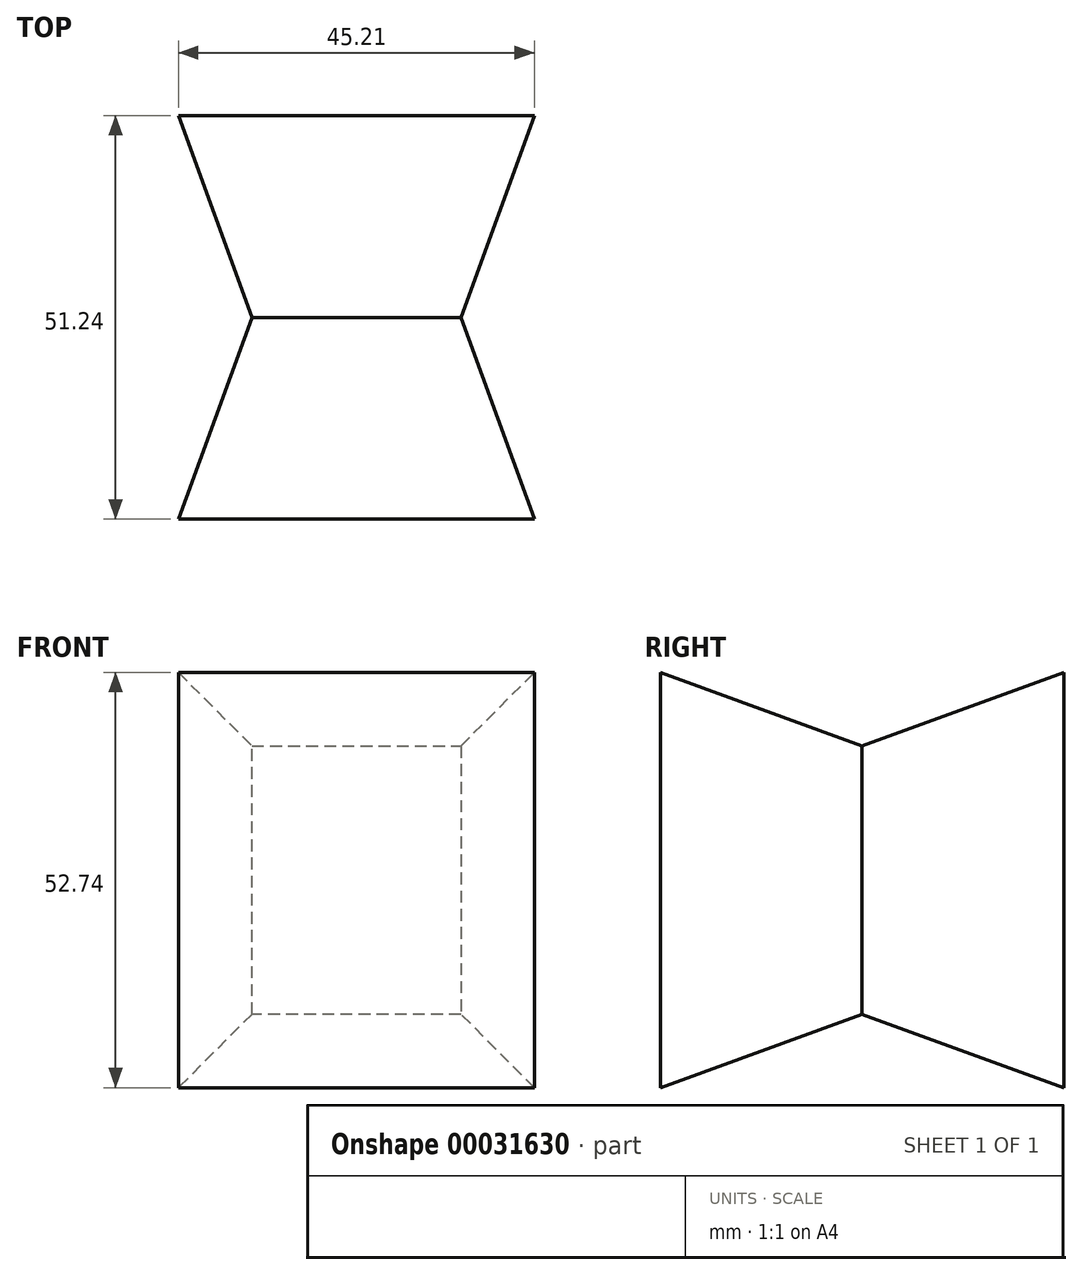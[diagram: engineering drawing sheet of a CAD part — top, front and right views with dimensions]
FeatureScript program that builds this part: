
annotation { "Feature Type Name" : "Feature", "Feature Type Description" : "" }
export const myFeature = defineFeature(function(context is Context, id is Id, definition is map)
    precondition{}
    {
        {
            var Q0;
            Q0=qCreatedBy(makeId("Front.planeOp"),FACE);
            var sketch = newSketch(context, id + "F0", { "sketchPlane" : qUnion([Q0])});
            skLineSegment(sketch, "E0.bottom", {"start": v(0, 0) * mm, "end": v(26.55, 0) * mm});
            skLineSegment(sketch, "E0.top", {"start": v(0, 34.08) * mm, "end": v(26.55, 34.08) * mm});
            skLineSegment(sketch, "E0.left", {"start": v(0, 0) * mm, "end": v(0, 34.08) * mm});
            skLineSegment(sketch, "E0.right", {"start": v(26.55, 0) * mm, "end": v(26.55, 34.08) * mm});
            skSolve(sketch);
        }
        {
            var Q0;
            Q0=makeQuery(id+"F0.imprint","IMPRINT",FACE,{"disambiguationData":[TD([[makeQuery(id+"F0.imprint","IMPRINT",EDGE,{"derivedFrom":sQuery(id+"F0.wireOp",EDGE,"E0.bottom")}),1.0]])]});
            extrude(context, id + "F1", {"entities" : qUnion([Q0]), "endBound" : BoundingType.SYMMETRIC, "depth" : 51.25 * mm, "hasDraft" : true, "draftAngle" : 20 * degree});
        }
    });
